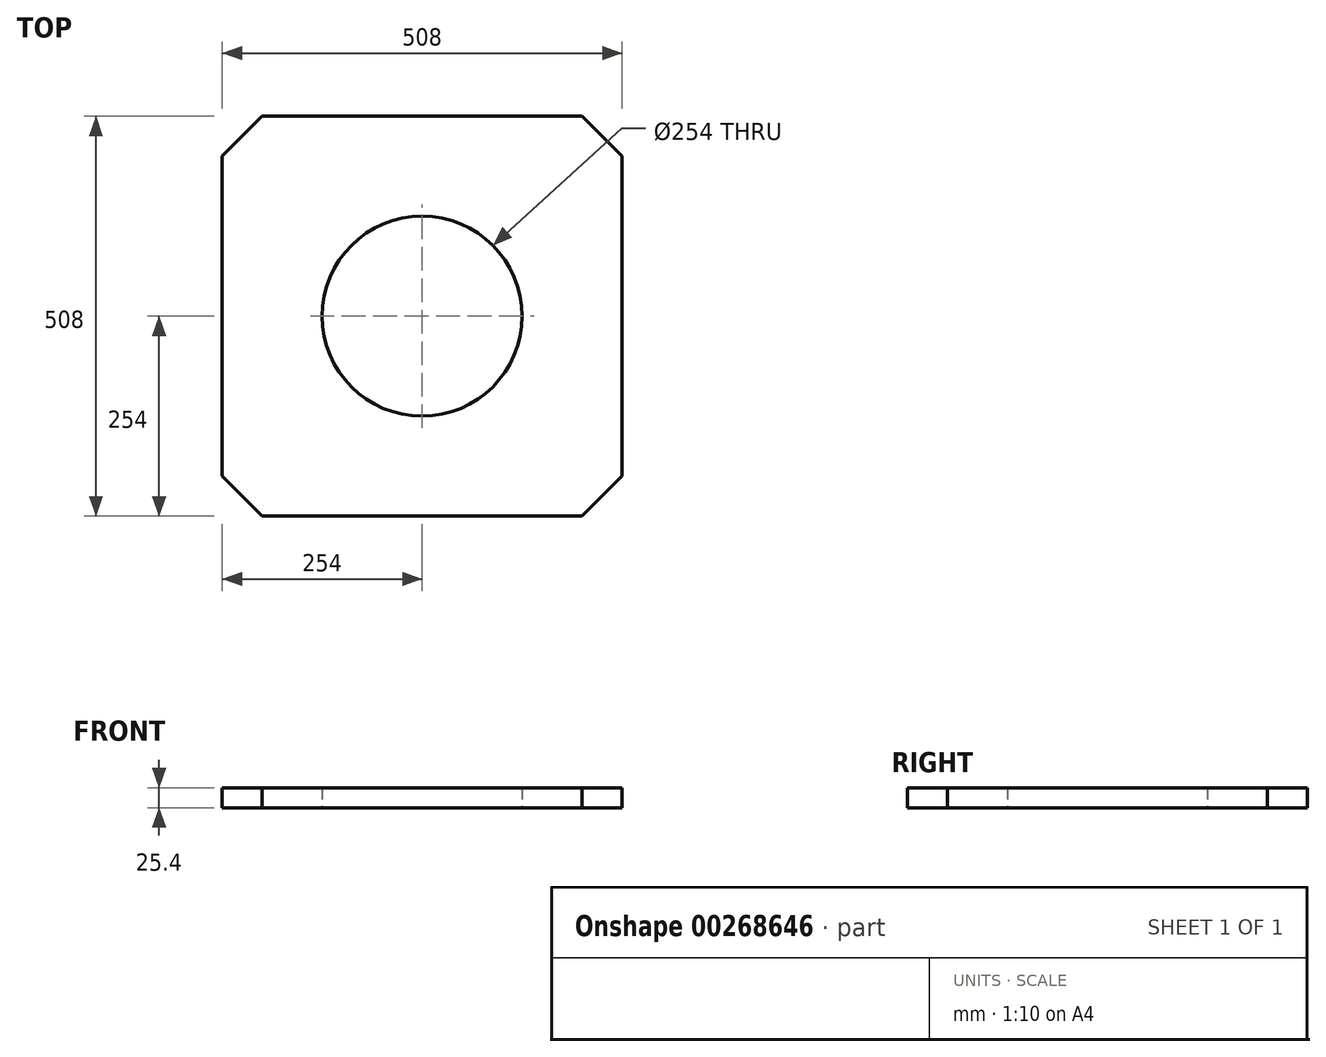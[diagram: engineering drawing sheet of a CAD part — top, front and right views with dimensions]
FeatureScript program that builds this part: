
annotation { "Feature Type Name" : "Feature", "Feature Type Description" : "" }
export const myFeature = defineFeature(function(context is Context, id is Id, definition is map)
    precondition{}
    {
        {
            var Q0;
            Q0=qCreatedBy(makeId("Top.planeOp"),FACE);
            var sketch = newSketch(context, id + "F0", { "sketchPlane" : qUnion([Q0])});
            skLineSegment(sketch, "E0.bottom", {"start": v(-254, 254) * mm, "end": v(254, 254) * mm});
            skLineSegment(sketch, "E0.top", {"start": v(-254, -254) * mm, "end": v(254, -254) * mm});
            skLineSegment(sketch, "E0.left", {"start": v(-254, 254) * mm, "end": v(-254, -254) * mm});
            skLineSegment(sketch, "E0.right", {"start": v(254, 254) * mm, "end": v(254, -254) * mm});
            skPoint(sketch, "E0.middle", {"position": v(0, 0) * mm});
            skCircle(sketch, "E1", {"center": v(0, 0) * mm, "radius": 127 * mm});
            skSolve(sketch);
        }
        {
            var Q0;
            Q0=makeQuery(id+"F0.imprint","IMPRINT",FACE,{"disambiguationData":[TD([[makeQuery(id+"F0.imprint","IMPRINT",EDGE,{"derivedFrom":sQuery(id+"F0.wireOp",EDGE,"E0.bottom")}),-1.0]])]});
            extrude(context, id + "F1", {"entities" : qUnion([Q0]), "depth" : 25.4 * mm});
        }
        {
            var Q0;
            Q0=makeQuery(id+"F1.opExtrude","SWEPT_EDGE",EDGE,{"disambiguationData":[OSD([sQuery(id+"F0.wireOp",EDGE,"E0.top"),sQuery(id+"F0.wireOp",EDGE,"E0.left")])]});
            var Q1;
            Q1=makeQuery(id+"F1.opExtrude","SWEPT_EDGE",EDGE,{"disambiguationData":[OSD([sQuery(id+"F0.wireOp",EDGE,"E0.top"),sQuery(id+"F0.wireOp",EDGE,"E0.right")])]});
            var Q2;
            Q2=makeQuery(id+"F1.opExtrude","SWEPT_EDGE",EDGE,{"disambiguationData":[OSD([sQuery(id+"F0.wireOp",EDGE,"E0.bottom"),sQuery(id+"F0.wireOp",EDGE,"E0.right")])]});
            var Q3;
            Q3=makeQuery(id+"F1.opExtrude","SWEPT_EDGE",EDGE,{"disambiguationData":[OSD([sQuery(id+"F0.wireOp",EDGE,"E0.bottom"),sQuery(id+"F0.wireOp",EDGE,"E0.left")])]});
            chamfer(context, id + "F2", {"entities" : qUnion([Q0, Q1, Q2, Q3]), "width" : 50.8 * mm, "tangentPropagation" : true});
        }
    });
